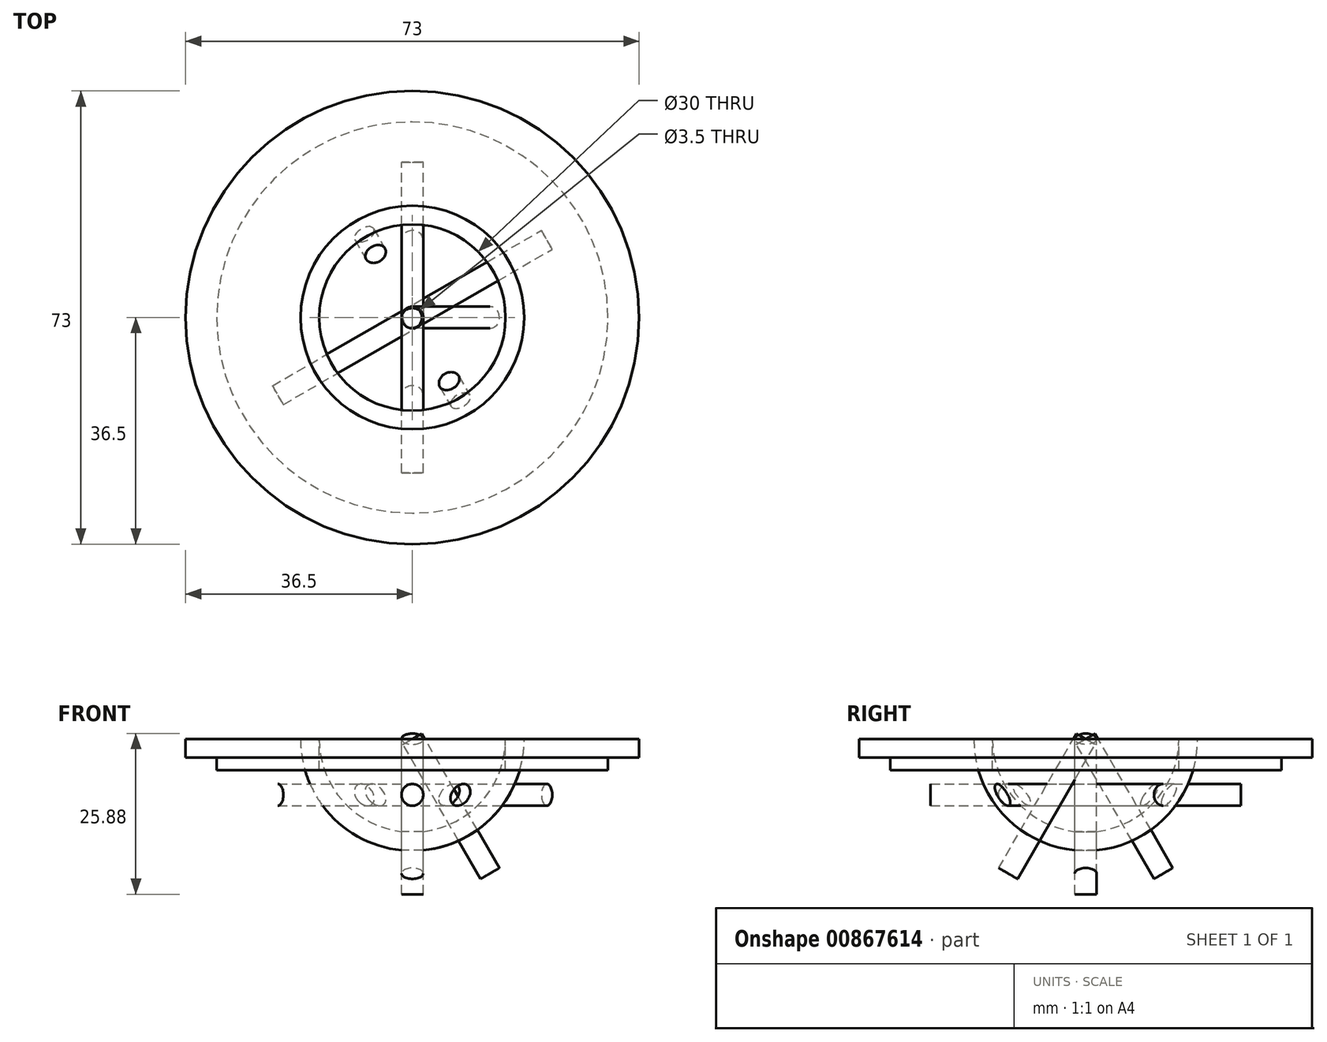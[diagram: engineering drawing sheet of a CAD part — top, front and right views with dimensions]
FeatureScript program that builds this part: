
annotation { "Feature Type Name" : "Feature", "Feature Type Description" : "" }
export const myFeature = defineFeature(function(context is Context, id is Id, definition is map)
    precondition{}
    {
        {
            var Q0;
            Q0=qCreatedBy(makeId("Front.planeOp"),FACE);
            var sketch = newSketch(context, id + "F0", { "sketchPlane" : qUnion([Q0])});
            skArc(sketch, "E0", {"start": v(-15, 0) * mm, "mid": v(-10.6, -10.6) * mm, "end": v(0, -15) * mm});
            skArc(sketch, "E1", {"start": v(-18, 0) * mm, "mid": v(-12.73, -12.73) * mm, "end": v(0, -18) * mm});
            skLineSegment(sketch, "E2", {"start": v(-24.93, 0) * mm, "end": v(20.1, 0) * mm, "construction": true});
            skLineSegment(sketch, "E3", {"start": v(0, 12.63) * mm, "end": v(0, -22.24) * mm, "construction": true});
            skPoint(sketch, "E3.endSnap0", {"position": v(0, -18) * mm});
            skLineSegment(sketch, "E4", {"start": v(0, -15) * mm, "end": v(0, -18) * mm});
            skLineSegment(sketch, "E5", {"start": v(-15, 0) * mm, "end": v(-18, 0) * mm});
            skSolve(sketch);
        }
        {
            var Q0;
            Q0=makeQuery(id+"F0.imprint","IMPRINT",FACE,{"disambiguationData":[TD([[makeQuery(id+"F0.imprint","IMPRINT",EDGE,{"derivedFrom":sQuery(id+"F0.wireOp",EDGE,"E0")}),-1.0]])]});
            var Q1;
            Q1=sQuery(id+"F0.wireOp",EDGE,"E3");
            revolve(context, id + "F1", {"surfaceOperationType" : NewSurfaceOperationType.NEW, "entities" : qUnion([Q0]), "axis" : qUnion([Q1]), "revolveType" : RevolveType.FULL});
        }
        {
            var Q0;
            Q0=makeQuery(id+"F1.opRevolve","SWEPT_FACE",FACE,{"disambiguationData":[OSD([sQuery(id+"F0.wireOp",EDGE,"E5")])]});
            var sketch = newSketch(context, id + "F2", { "sketchPlane" : qUnion([Q0])});
            skCircle(sketch, "E6", {"center": v(0, 0) * mm, "radius": 31.5 * mm});
            skCircle(sketch, "E7", {"center": v(0, 0) * mm, "radius": 15 * mm});
            skCircle(sketch, "E8", {"center": v(0, 0) * mm, "radius": 36.5 * mm});
            skSolve(sketch);
        }
        {
            var Q0;
            Q0=makeQuery(id+"F2.imprint","IMPRINT",FACE,{"disambiguationData":[TD([[makeQuery(id+"F2.imprint","IMPRINT",EDGE,{"derivedFrom":sQuery(id+"F2.wireOp",EDGE,"E7")}),-1.0]])]});
            var Q1;
            Q1=makeQuery(id+"F2.imprint","IMPRINT",FACE,{"disambiguationData":[TD([[makeQuery(id+"F2.imprint","IMPRINT",EDGE,{"derivedFrom":sQuery(id+"F2.wireOp",EDGE,"E6")}),1.0]])]});
            extrude(context, id + "F3", {"entities" : qUnion([Q0, Q1]), "oppositeDirection" : true, "depth" : 5 * mm, "offsetDistance" : 25 * mm});
        }
        {
            var Q0;
            Q0=makeQuery(id+"F2.imprint","IMPRINT",FACE,{"disambiguationData":[TD([[makeQuery(id+"F2.imprint","IMPRINT",EDGE,{"derivedFrom":sQuery(id+"F2.wireOp",EDGE,"E6")}),-1.0]])]});
            extrude(context, id + "F4", {"entities" : qUnion([Q0]), "operationType" : NewBodyOperationType.ADD, "oppositeDirection" : true, "depth" : 3 * mm, "offsetDistance" : 25 * mm});
        }
        {
            var Q0;
            Q0=qCreatedBy(makeId("Top.planeOp"),FACE);
            var sketch = newSketch(context, id + "F5", { "sketchPlane" : qUnion([Q0])});
            skCircle(sketch, "E9", {"center": v(0, 0) * mm, "radius": 1.75 * mm});
            skSolve(sketch);
        }
        {
            var Q0;
            Q0 = qSketchRegion(id + "F5", true);
            extrude(context, id + "F6", {"entities" : qUnion([Q0]), "oppositeDirection" : true, "depth" : 25 * mm, "offsetDistance" : 25 * mm});
        }
        {
            var Q0;
            Q0=makeQuery(id+"F6.opExtrude","SWEPT_BODY",BODY,{"disambiguationData":[OSD([sQuery(id+"F5.wireOp",EDGE,"E9")])]});
            var Q1;
            Q1=sQuery(id+"F0.wireOp",EDGE,"E3");
            var Q2;
            Q2=sQuery(id+"F0.wireOp",EDGE,"E2");
            transform(context, id + "F7", {"entities" : qUnion([Q0]), "transformType" : TransformType.ROTATION, "transformAxis" : qUnion([Q2]), "angle" : 30 * degree, "makeCopy" : true});
        }
        {
            var Q0;
            Q0=makeQuery(id+"F6.opExtrude","SWEPT_BODY",BODY,{"disambiguationData":[OSD([sQuery(id+"F5.wireOp",EDGE,"E9")])]});
            var Q1;
            Q1=sQuery(id+"F0.wireOp",EDGE,"E2");
            transform(context, id + "F8", {"entities" : qUnion([Q0]), "transformType" : TransformType.ROTATION, "transformAxis" : qUnion([Q1]), "angle" : 30 * degree, "oppositeDirection" : true, "makeCopy" : true});
        }
        {
            var Q0;
            Q0=makeQuery(id+"F7.opPattern","COPY",BODY,{"derivedFrom":makeQuery(id+"F6.opExtrude","SWEPT_BODY",BODY,{"disambiguationData":[OSD([sQuery(id+"F5.wireOp",EDGE,"E9")])]}),"instanceName":"1"});
            var Q1;
            Q1=sQuery(id+"F0.wireOp",EDGE,"E3");
            transform(context, id + "F9", {"entities" : qUnion([Q0]), "transformType" : TransformType.ROTATION, "transformAxis" : qUnion([Q1]), "angle" : 90 * degree, "makeCopy" : true});
        }
        {
            var Q0;
            Q0=makeQuery(id+"F6.opExtrude","SWEPT_BODY",BODY,{"disambiguationData":[OSD([sQuery(id+"F5.wireOp",EDGE,"E9")])]});
            transform(context, id + "F10", {"entities" : qUnion([Q0]), "transformType" : TransformType.TRANSLATION_3D, "dx" : 0 * mm, "dy" : 0 * mm, "dz" : 7 * mm, "makeCopy" : true});
        }
        {
            var Q0;
            Q0=makeQuery(id+"F10.opPattern","COPY",BODY,{"derivedFrom":makeQuery(id+"F6.opExtrude","SWEPT_BODY",BODY,{"disambiguationData":[OSD([sQuery(id+"F5.wireOp",EDGE,"E9")])]}),"instanceName":"1"});
            var Q1;
            Q1=sQuery(id+"F0.wireOp",EDGE,"E3");
            transform(context, id + "F11", {"entities" : qUnion([Q0]), "transformType" : TransformType.ROTATION, "transformAxis" : qUnion([Q1]), "angle" : 45 * degree, "makeCopy" : false});
        }
        {
            var Q0;
            Q0=qCreatedBy(makeId("Front.planeOp"),FACE);
            var sketch = newSketch(context, id + "F12", { "sketchPlane" : qUnion([Q0])});
            skCircle(sketch, "E10", {"center": v(0, -9) * mm, "radius": 1.75 * mm});
            skSolve(sketch);
        }
        {
            var Q0;
            Q0 = qSketchRegion(id + "F12", true);
            extrude(context, id + "F13", {"entities" : qUnion([Q0]), "endBound" : BoundingType.SYMMETRIC, "depth" : 50 * mm, "offsetDistance" : 25 * mm});
        }
        {
            var Q0;
            Q0=makeQuery(id+"F13.opExtrude","SWEPT_BODY",BODY,{"disambiguationData":[OSD([sQuery(id+"F12.wireOp",EDGE,"E10")])]});
            var Q1;
            Q1=sQuery(id+"F0.wireOp",EDGE,"E3");
            transform(context, id + "F14", {"entities" : qUnion([Q0]), "transformType" : TransformType.ROTATION, "transformAxis" : qUnion([Q1]), "angle" : 60 * degree, "makeCopy" : true});
        }
        {
            var Q0;
            Q0=makeQuery(id+"F14.opPattern","COPY",BODY,{"derivedFrom":makeQuery(id+"F13.opExtrude","SWEPT_BODY",BODY,{"disambiguationData":[OSD([sQuery(id+"F12.wireOp",EDGE,"E10")])]}),"instanceName":"1"});
            var Q1;
            Q1=sQuery(id+"F0.wireOp",EDGE,"E3");
            transform(context, id + "F15", {"entities" : qUnion([Q0]), "transformType" : TransformType.ROTATION, "transformAxis" : qUnion([Q1]), "angle" : 60 * degree, "makeCopy" : true});
        }
        {
            var Q0;
            Q0=makeQuery(id+"F15.opPattern","COPY",BODY,{"derivedFrom":makeQuery(id+"F14.opPattern","COPY",BODY,{"derivedFrom":makeQuery(id+"F13.opExtrude","SWEPT_BODY",BODY,{"disambiguationData":[OSD([sQuery(id+"F12.wireOp",EDGE,"E10")])]}),"instanceName":"1"}),"instanceName":"1"});
            var Q1;
            Q1=sQuery(id+"F0.wireOp",EDGE,"E3");
            transform(context, id + "F16", {"entities" : qUnion([Q0]), "transformType" : TransformType.ROTATION, "transformAxis" : qUnion([Q1]), "angle" : 30 * degree, "makeCopy" : false});
        }
        {
            var Q0;
            Q0=makeQuery(id+"F15.opPattern","COPY",BODY,{"derivedFrom":makeQuery(id+"F14.opPattern","COPY",BODY,{"derivedFrom":makeQuery(id+"F13.opExtrude","SWEPT_BODY",BODY,{"disambiguationData":[OSD([sQuery(id+"F12.wireOp",EDGE,"E10")])]}),"instanceName":"1"}),"instanceName":"1"});
            var Q1;
            Q1=makeQuery(id+"F10.opPattern","COPY",BODY,{"derivedFrom":makeQuery(id+"F6.opExtrude","SWEPT_BODY",BODY,{"disambiguationData":[OSD([sQuery(id+"F5.wireOp",EDGE,"E9")])]}),"instanceName":"1"});
            var Q2;
            Q2=makeQuery(id+"F1.opRevolve","SWEPT_BODY",BODY,{"disambiguationData":[OSD([sQuery(id+"F0.wireOp",EDGE,"E0"),sQuery(id+"F0.wireOp",EDGE,"E1"),sQuery(id+"F0.wireOp",EDGE,"E4"),sQuery(id+"F0.wireOp",EDGE,"E5")])]});
            booleanBodies(context, id + "F17", {"operationType" : BooleanOperationType.SUBTRACTION, "tools" : qUnion([Q0, Q1]), "targets" : qUnion([Q2])});
        }
    });
